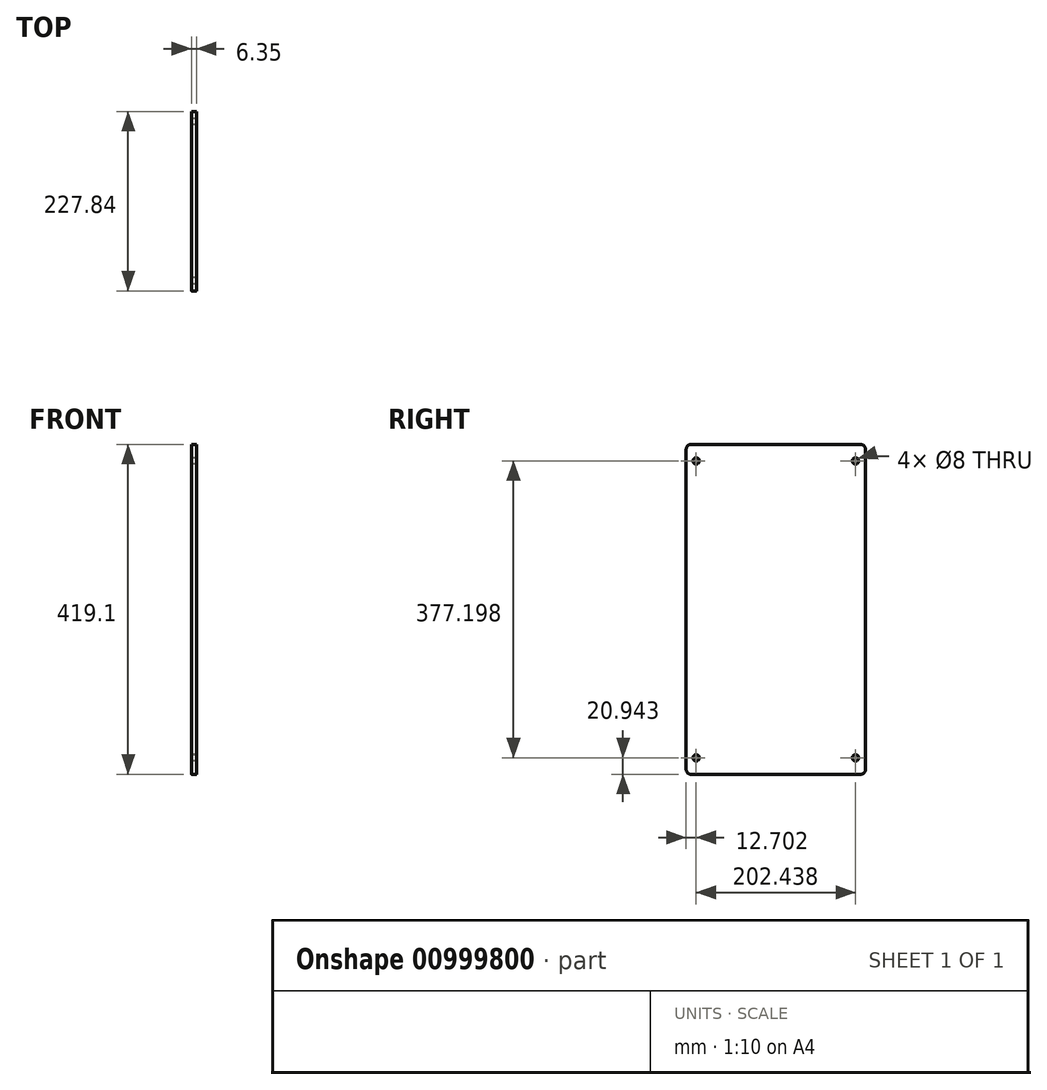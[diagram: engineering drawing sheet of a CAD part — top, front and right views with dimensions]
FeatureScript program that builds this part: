
annotation { "Feature Type Name" : "Feature", "Feature Type Description" : "" }
export const myFeature = defineFeature(function(context is Context, id is Id, definition is map)
    precondition{}
    {
        {
            var Q0;
            Q0=qCreatedBy(makeId("Right.planeOp"),FACE);
            var sketch = newSketch(context, id + "F0", { "sketchPlane" : qUnion([Q0])});
            skLineSegment(sketch, "E0.bottom", {"start": v(-107.4, 368.07) * mm, "end": v(107.74, 368.07) * mm});
            skLineSegment(sketch, "E0.top", {"start": v(-107.4, -51.03) * mm, "end": v(107.74, -51.03) * mm});
            skLineSegment(sketch, "E0.left", {"start": v(-113.75, 361.72) * mm, "end": v(-113.75, -44.68) * mm});
            skLineSegment(sketch, "E0.right", {"start": v(114.1, 361.72) * mm, "end": v(114.1, -44.68) * mm});
            skCircle(sketch, "E1", {"center": v(101.4, 347.11) * mm, "radius": 4 * mm});
            skCircle(sketch, "E2", {"center": v(-101.05, 347.11) * mm, "radius": 4 * mm});
            skCircle(sketch, "E3", {"center": v(101.4, -30.09) * mm, "radius": 4 * mm});
            skCircle(sketch, "E4", {"center": v(-101.05, -30.07) * mm, "radius": 4 * mm});
            skPoint(sketch, "E5.visualSharp", {"position": v(114.1, 368.07) * mm});
            skArc(sketch, "E5.filletArc", {"start": v(114.1, 361.72) * mm, "mid": v(112.23, 366.2) * mm, "end": v(107.74, 368.07) * mm});
            skPoint(sketch, "E6.visualSharp", {"position": v(-113.75, 368.07) * mm});
            skArc(sketch, "E6.filletArc", {"start": v(-107.4, 368.07) * mm, "mid": v(-111.89, 366.2) * mm, "end": v(-113.75, 361.72) * mm});
            skPoint(sketch, "E7.visualSharp", {"position": v(-113.75, -51.03) * mm});
            skArc(sketch, "E7.filletArc", {"start": v(-113.75, -44.68) * mm, "mid": v(-111.89, -49.17) * mm, "end": v(-107.4, -51.03) * mm});
            skPoint(sketch, "E8.visualSharp", {"position": v(114.1, -51.03) * mm});
            skArc(sketch, "E8.filletArc", {"start": v(107.74, -51.03) * mm, "mid": v(112.23, -49.17) * mm, "end": v(114.1, -44.68) * mm});
            skSolve(sketch);
        }
        {
            var Q0;
            Q0=makeQuery(id+"F0.imprint","IMPRINT",FACE,{"disambiguationData":[TD([[makeQuery(id+"F0.imprint","IMPRINT",EDGE,{"derivedFrom":sQuery(id+"F0.wireOp",EDGE,"E0.bottom")}),-1.0]])]});
            extrude(context, id + "F1", {"entities" : qUnion([Q0]), "depth" : 6.35 * mm, "offsetDistance" : 25.4 * mm});
        }
    });
